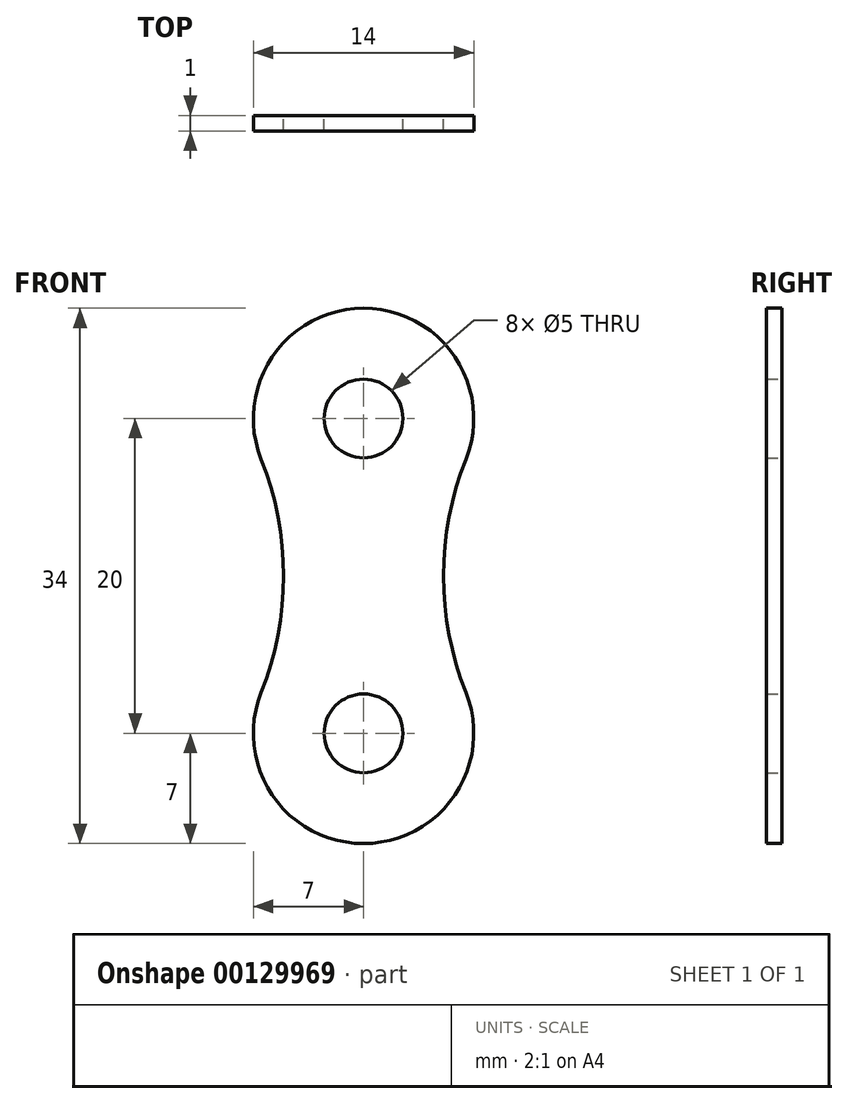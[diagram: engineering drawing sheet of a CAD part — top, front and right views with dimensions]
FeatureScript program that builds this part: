
annotation { "Feature Type Name" : "Feature", "Feature Type Description" : "" }
export const myFeature = defineFeature(function(context is Context, id is Id, definition is map)
    precondition{}
    {
        {
            var Q0;
            Q0=qCreatedBy(makeId("Front.planeOp"),FACE);
            var sketch = newSketch(context, id + "F0", { "sketchPlane" : qUnion([Q0])});
            skArc(sketch, "E0", {"start": v(6.5, -2.6) * mm, "mid": v(0, 7) * mm, "end": v(-6.5, -2.6) * mm});
            skArc(sketch, "E1", {"start": v(-6.5, -17.4) * mm, "mid": v(0, -27) * mm, "end": v(6.5, -17.4) * mm});
            skArc(sketch, "E2", {"start": v(-6.5, -17.4) * mm, "mid": v(-5.08, -10) * mm, "end": v(-6.5, -2.6) * mm});
            skArc(sketch, "E3", {"start": v(6.5, -2.6) * mm, "mid": v(5.08, -10) * mm, "end": v(6.5, -17.4) * mm});
            skCircle(sketch, "E4", {"center": v(0, 0) * mm, "radius": 2.5 * mm});
            skCircle(sketch, "E5", {"center": v(0, -20) * mm, "radius": 2.5 * mm});
            skSolve(sketch);
        }
        {
            var Q0;
            Q0=makeQuery(id+"F0.imprint","IMPRINT",FACE,{"disambiguationData":[TD([[makeQuery(id+"F0.imprint","IMPRINT",EDGE,{"derivedFrom":sQuery(id+"F0.wireOp",EDGE,"E0")}),1.0]])]});
            extrude(context, id + "F1", {"entities" : qUnion([Q0]), "depth" : 1 * mm});
        }
    });
